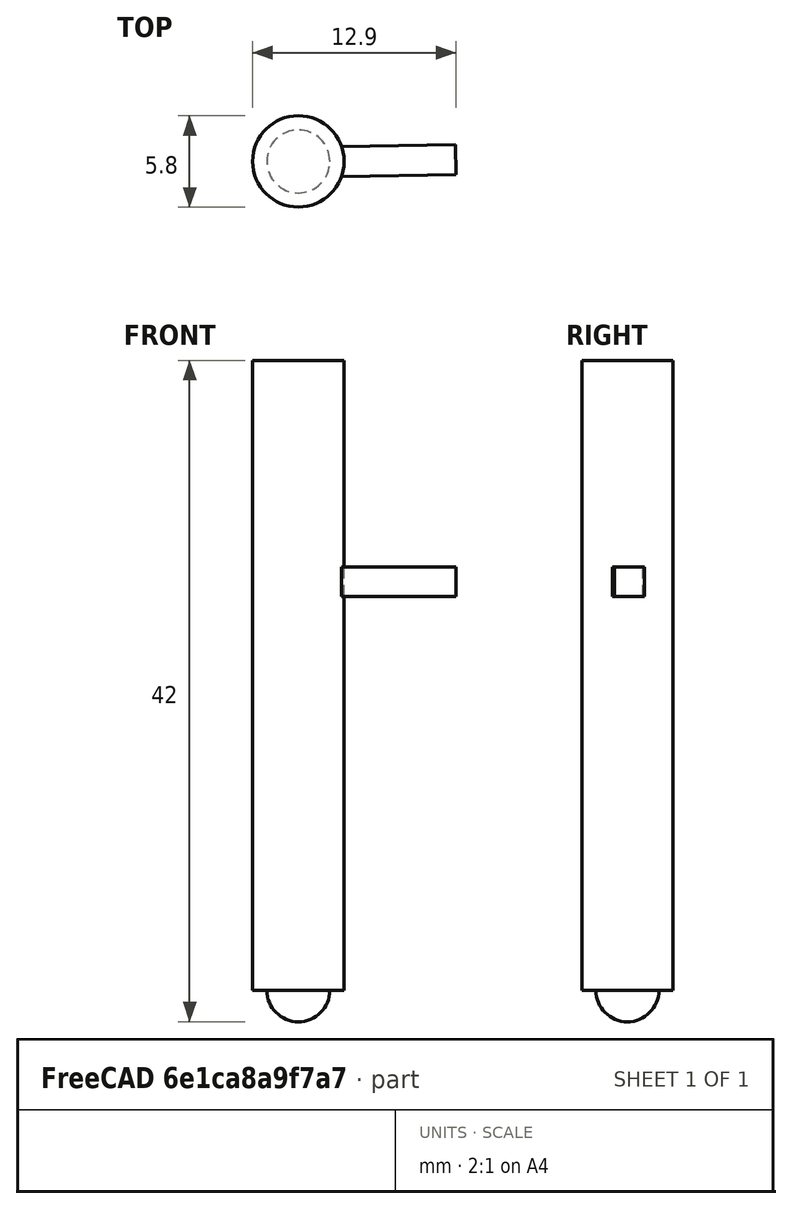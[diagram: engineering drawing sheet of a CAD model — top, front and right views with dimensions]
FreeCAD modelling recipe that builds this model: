
FCSTD DOCUMENT  (FreeCAD 0.16R6712 (Git))
Label: DOIGT_INT
License: All rights reserved
LicenseURL: http://en.wikipedia.org/wiki/All_rights_reserved
objects: Part::Fuse×2, Sketcher::SketchObject×1, PartDesign::Pad×1, Part::Box×1, Part::Sphere×1, Mesh::Feature×1
note: 7 computed .brp shape members not serialized (recipe doc carries the construction recipe); baked Part::Feature solids carry a one-line shape summary decoded from their .brp

FEATURE [Sketcher::SketchObject] Sketch
  sketch-geometry (1):
    g0: Circle CenterX=0 CenterY=0 CenterZ=0 NormalX=0 NormalY=0 NormalZ=1 Radius=2.9
  constraints (2):
    c: Coincident(g0,g-1)
    c: Radius(g0) = 2.9
FEATURE [PartDesign::Pad] Pad
  Length = 40
  Length2 = 100
  Sketch = -> Sketch
  Type = 0
FEATURE [Part::Box] Box  label="Cube"
  Height = 1.9
  Length = 10
  Placement = pos=(0,-1,25) rot=(0,0,1;0.017453rad)
  Width = 1.9
FEATURE [Part::Fuse] Fusion
  Base = -> Pad
  Tool = -> Box
FEATURE [Part::Sphere] Sphere  label="Sphère"
  Angle1 = -90
  Angle2 = 90
  Angle3 = 360
  Radius = 2
FEATURE [Part::Fuse] Fusion001
  Base = -> Pad
  Tool = -> Sphere
FEATURE [Mesh::Feature] Mesh  label="Fusion001 (Meshed)"
